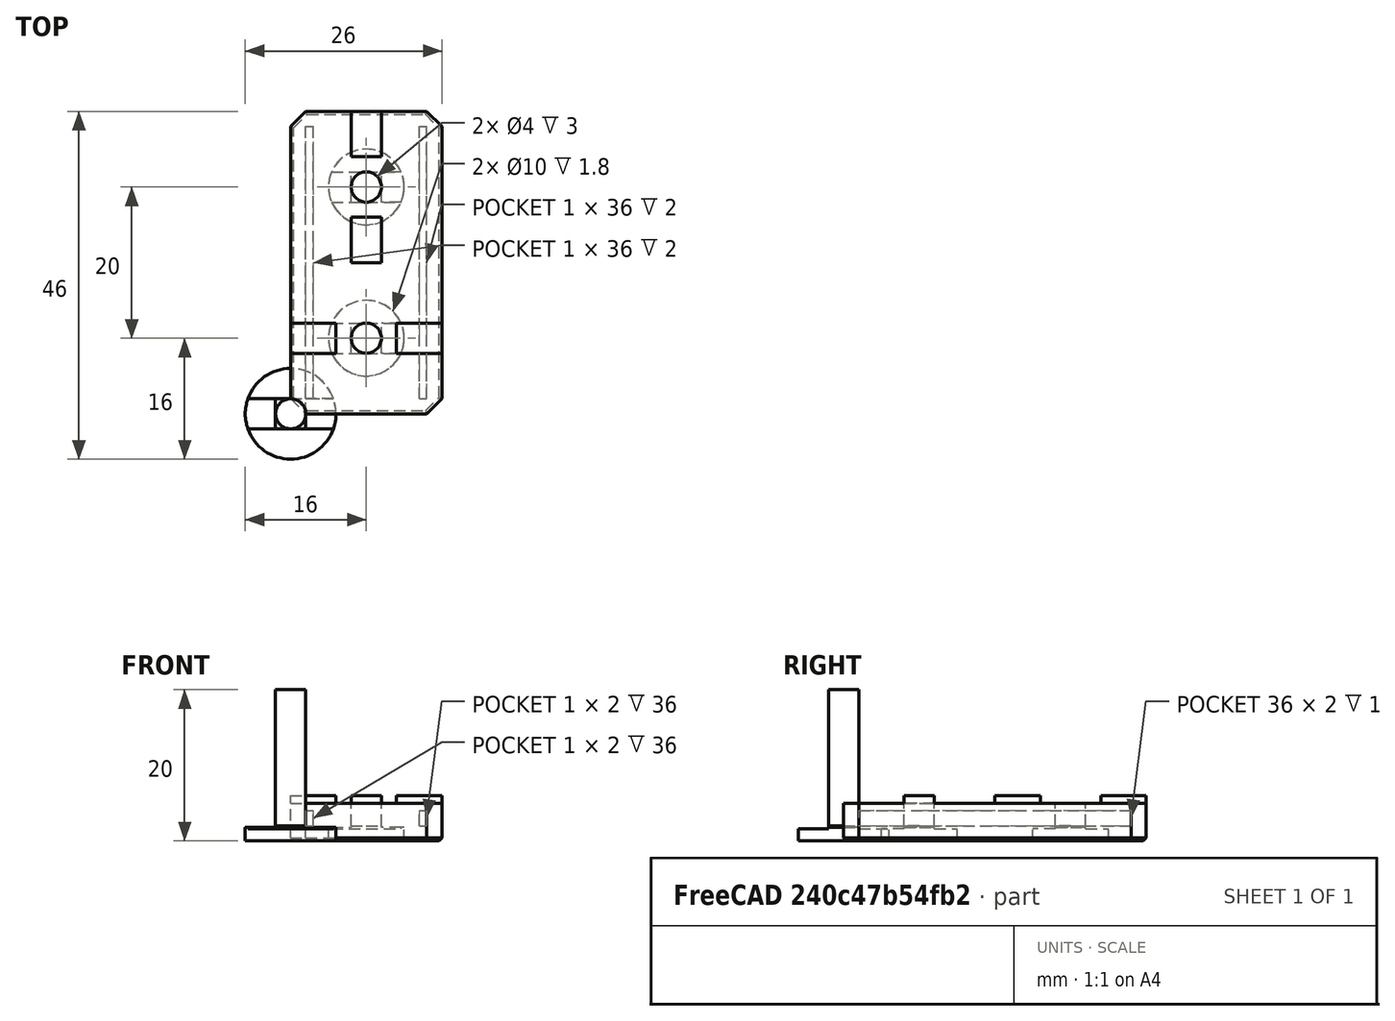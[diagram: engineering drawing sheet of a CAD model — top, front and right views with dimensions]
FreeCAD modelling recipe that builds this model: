
FCSTD DOCUMENT  (FreeCAD 0.18R14555 (Git shallow))
Label: y-supporter
License: All rights reserved
LicenseURL: http://en.wikipedia.org/wiki/All_rights_reserved
objects: Part::Box×11, Part::MultiFuse×4, Part::Cylinder×4, Part::Cut×4, Part::Chamfer×2, Part::Feature×2, Part::MultiCommon×2
note: 29 computed .brp shape members not serialized (recipe doc carries the construction recipe); baked Part::Feature solids carry a one-line shape summary decoded from their .brp

FEATURE [Part::Box] Box  label="Cube"
  AttacherType = Attacher::AttachEngine3D
  Height = 1
  Length = 4
  Placement = pos=(8,20,5) rot=(0,0,1;0rad)
  Width = 6
FEATURE [Part::Box] Box001  label="Cube001"
  AttacherType = Attacher::AttachEngine3D
  Height = 1
  Length = 6
  Placement = pos=(0,8,5) rot=(0,0,1;0rad)
  Width = 4
FEATURE [Part::Box] Box002  label="Cube002"
  AttacherType = Attacher::AttachEngine3D
  Height = 5
  Length = 20
  Width = 40
FEATURE [Part::Box] Box003  label="Cube003"
  AttacherType = Attacher::AttachEngine3D
  Height = 1
  Length = 6
  Placement = pos=(14,8,5) rot=(0,0,1;0rad)
  Width = 4
FEATURE [Part::Box] Box004  label="Cube004"
  AttacherType = Attacher::AttachEngine3D
  Height = 1
  Length = 4
  Placement = pos=(8,34,5) rot=(0,0,1;0rad)
  Width = 6
FEATURE [Part::MultiFuse] Fusion
  Shapes = -> [Box004,Box003,Box002,Box001,Box]
FEATURE [Part::Chamfer] Chamfer
  Base = -> Fusion
  Edges = 4 edges r=2: [Edge1,Edge5,Edge8,Edge31]
FEATURE [Part::Chamfer] Chamfer001
  Base = -> Chamfer
  Edges = 8 edges r=0.4: [Edge4,Edge29,Edge34,Edge35,Edge36,Edge37,Edge38,Edge39]
FEATURE [Part::Cylinder] Cylinder
  Angle = 360
  AttacherType = Attacher::AttachEngine3D
  Height = 20
  Radius = 2
FEATURE [Part::Cylinder] Cylinder001
  Angle = 360
  AttacherType = Attacher::AttachEngine3D
  Height = 2
  Radius = 6
FEATURE [Part::Box] Box005  label="Cube005"
  AttacherType = Attacher::AttachEngine3D
  Height = 0.4
  Length = 20
  Placement = pos=(-10,2,1.6) rot=(0,0,1;0rad)
  Width = 10
FEATURE [Part::Box] Box006  label="Cube006"
  AttacherType = Attacher::AttachEngine3D
  Height = 0.2
  Length = 10
  Placement = pos=(-12,-10,1.8) rot=(0,0,1;0rad)
  Width = 20
FEATURE [Part::Box] Box007  label="Cube007"
  AttacherType = Attacher::AttachEngine3D
  Height = 0.4
  Length = 20
  Placement = pos=(-10,-12,1.6) rot=(0,0,1;0rad)
  Width = 10
FEATURE [Part::Box] Box008  label="Cube008"
  AttacherType = Attacher::AttachEngine3D
  Height = 0.2
  Length = 10
  Placement = pos=(2,-10,1.8) rot=(0,0,1;0rad)
  Width = 20
FEATURE [Part::MultiFuse] Fusion001
  Shapes = -> [Box008,Box005,Box007,Box006]
FEATURE [Part::Cut] Cut
  Base = -> Cylinder001
  Tool = -> Fusion001
FEATURE [Part::MultiFuse] Fusion002
  Shapes = -> [Cylinder,Cut]
FEATURE [Part::Feature] Fusion002001  label="Fusion003"
  Placement = pos=(10,10,0) rot=(0,0,1;0rad)
  shape: bbox 12 x 12 x 20 mm, 21 faces (baked)
FEATURE [Part::Feature] Fusion002002  label="Fusion004"
  Placement = pos=(10,30,0) rot=(0,0,1;0rad)
  shape: bbox 12 x 12 x 20 mm, 21 faces (baked)
FEATURE [Part::Cylinder] Cylinder002
  Angle = 360
  AttacherType = Attacher::AttachEngine3D
  Height = 10
  Placement = pos=(10,10,0) rot=(0,0,1;0rad)
  Radius = 5
FEATURE [Part::Cylinder] Cylinder003
  Angle = 360
  AttacherType = Attacher::AttachEngine3D
  Height = 10
  Placement = pos=(10,30,0) rot=(0,0,1;0rad)
  Radius = 5
FEATURE [Part::MultiCommon] Common
  Shapes = -> [Fusion002002,Cylinder003]
FEATURE [Part::MultiCommon] Common001
  Shapes = -> [Cylinder002,Fusion002001]
FEATURE [Part::Cut] Cut001
  Base = -> Chamfer001
  Tool = -> Common
FEATURE [Part::Cut] Cut002
  Base = -> Cut001
  Tool = -> Common001
FEATURE [Part::Box] Box009  label="Cube009"
  AttacherType = Attacher::AttachEngine3D
  Height = 2
  Length = 1
  Placement = pos=(2,2,2) rot=(0,0,1;0rad)
  Width = 36
FEATURE [Part::Box] Box010  label="Cube010"
  AttacherType = Attacher::AttachEngine3D
  Height = 2
  Length = 1
  Placement = pos=(17,2,2) rot=(0,0,1;0rad)
  Width = 36
FEATURE [Part::MultiFuse] Fusion002003
  Shapes = -> [Box010,Box009]
FEATURE [Part::Cut] Cut003
  Base = -> Cut002
  Tool = -> Fusion002003
